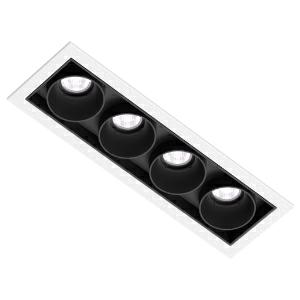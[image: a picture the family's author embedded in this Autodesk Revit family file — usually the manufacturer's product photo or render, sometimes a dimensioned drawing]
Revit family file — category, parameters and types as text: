
# Revit family: magiq_220-0734
name_source: partatom
category: Lighting Fixtures
units: mm (PartAtom-declared; Revit-internal decimal feet)

## family parameters
Cut with Voids When Loaded = No
Host = Face
Light Source = No
Part Type = Normal
Room Calculation Point = No
Round Connector Dimension = Use Diameter
Shared = No

## types (1)
- 220-0734-H27-U02-W11 (1 x LED, 880 lm, 13.3 W, 2700K)
    Apparent Load = 13 VA
    CIE Flux Codes = 98 99 99 100 75
    Color Rendering = 1A/90…99
    Color Temperature = 2700K
    Default Elevation = 1800 mm
    Description = MAGIQ
    Height = 0 mm  [stored 0 ft]
    Lamp = 1 x LED
    Lamp Light Flux = 880 lm
    Lamp Power = 13.3 W
    Lamp count = 1
    Length = 145 mm
    Luminous efficacy = 50 lm/W
    Manufacturer = Prolicht
    ModVariant = No
    Model = 220-0734
    Mounting Place = Ceiling
    Mounting Type = Recessed
    Number of Poles = 1
    OnlyDefault = Yes
    Power Factor = 1
    Product Name = MAGIQ
    Product group = Recessed spotlights
    ProductGroupID = 422
    Protection Class = Protection class
    Protection Degree = Degree of protection
    RLX_Detail_Level = 1
    RlxData = <blob elided: 362861 chars, md5=510a62bb>
    Socket = socket
    Standby Power = 0 W
    System Light Flux = 659 lm
    System Power = 13 W
    Type Comments = LED COLOUR DIR 2700 K (27),FRAME_COLOUR BLACK (02),BEAMWIDTH Super Spot (11)
    Type Image = 220-0734.jpg
    URL = http://relux.com
    VarID = 220-0734-h27-u02-w11
    Voltage = 0 V
    Weight = 0.00 kg
    Width = 45 mm

note: [stored X ft] marks values corroborated as IEEE doubles in the binary element streams (Revit-internal decimal feet)

## geometry (parser evidence)
native form markers: Blend x4, Sweep x11
no freeform markers — native parametric forms only
